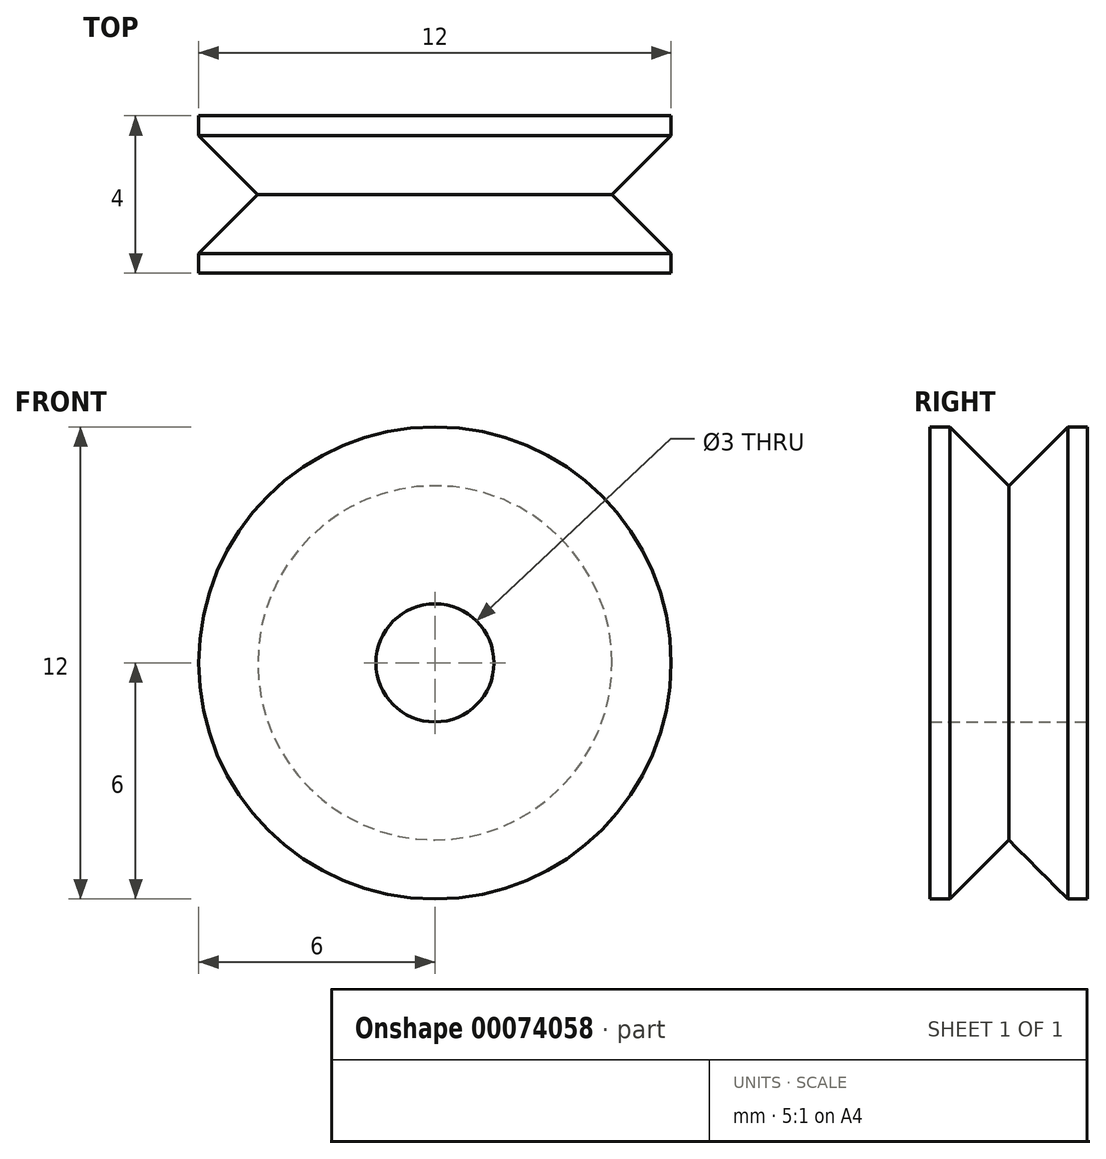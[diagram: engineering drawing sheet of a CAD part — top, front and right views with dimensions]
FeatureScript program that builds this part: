
annotation { "Feature Type Name" : "Feature", "Feature Type Description" : "" }
export const myFeature = defineFeature(function(context is Context, id is Id, definition is map)
    precondition{}
    {
        {
            var Q0;
            Q0=qCreatedBy(makeId("Front.planeOp"),FACE);
            var sketch = newSketch(context, id + "F0", { "sketchPlane" : qUnion([Q0])});
            skCircle(sketch, "E0", {"center": v(0, 0) * mm, "radius": 1.5 * mm});
            skCircle(sketch, "E1", {"center": v(0, 0) * mm, "radius": 6 * mm});
            skSolve(sketch);
        }
        {
            var Q0;
            Q0=makeQuery(id+"F0.imprint","IMPRINT",FACE,{"disambiguationData":[TD([[makeQuery(id+"F0.imprint","IMPRINT",EDGE,{"derivedFrom":sQuery(id+"F0.wireOp",EDGE,"E0")}),-1.0]])]});
            extrude(context, id + "F1", {"entities" : qUnion([Q0]), "depth" : 2 * mm});
        }
        {
            var Q0;
            Q0=makeQuery(id+"F1.opExtrude","CAP_EDGE",EDGE,{"disambiguationData":[OSD([sQuery(id+"F0.wireOp",EDGE,"E1")])],"isStart":true});
            chamfer(context, id + "F2", {"entities" : qUnion([Q0]), "width" : 1.5 * mm, "tangentPropagation" : true});
        }
        {
            var Q0;
            Q0=makeQuery(id+"F1.opExtrude","SWEPT_BODY",BODY,{"disambiguationData":[OSD([sQuery(id+"F0.wireOp",EDGE,"E0"),sQuery(id+"F0.wireOp",EDGE,"E1")])]});
            var Q1;
            Q1=qCreatedBy(makeId("Front.planeOp"),FACE);
            mirror(context, id + "F3", {"operationType" : NewBodyOperationType.ADD, "entities" : qUnion([Q0]), "mirrorPlane" : qUnion([Q1])});
        }
    });
